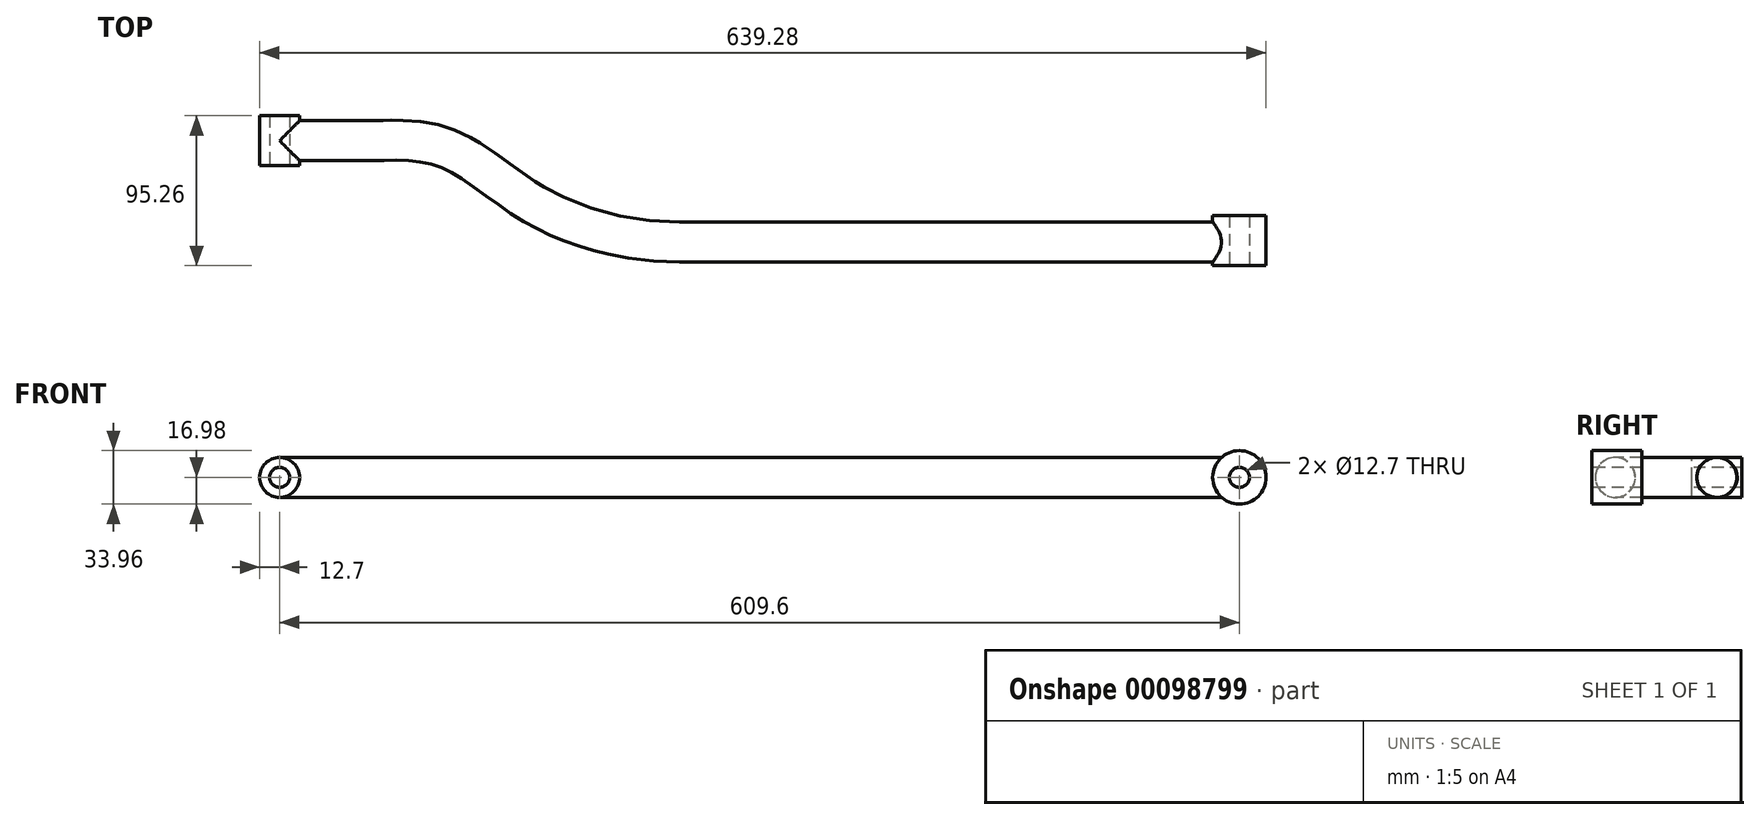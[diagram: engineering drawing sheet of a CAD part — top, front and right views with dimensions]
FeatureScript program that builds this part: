
annotation { "Feature Type Name" : "Feature", "Feature Type Description" : "" }
export const myFeature = defineFeature(function(context is Context, id is Id, definition is map)
    precondition{}
    {
        {
            var Q0;
            Q0=qCreatedBy(makeId("Front.planeOp"),FACE);
            var sketch = newSketch(context, id + "F0", { "sketchPlane" : qUnion([Q0])});
            skCircle(sketch, "E0", {"center": v(0, 0) * mm, "radius": 12.7 * mm});
            skSolve(sketch);
        }
        {
            var Q0;
            Q0=qCreatedBy(makeId("Right.planeOp"),FACE);
            var sketch = newSketch(context, id + "F1", { "sketchPlane" : qUnion([Q0])});
            skCircle(sketch, "E1", {"center": v(0, 0) * mm, "radius": 12.7 * mm});
            skSolve(sketch);
        }
        {
            var Q0;
            Q0=qCreatedBy(makeId("Top.planeOp"),FACE);
            var sketch = newSketch(context, id + "F2", { "sketchPlane" : qUnion([Q0])});
            skLineSegment(sketch, "E2", {"start": v(436.7, -63.5) * mm, "end": v(492.47, -63.5) * mm});
            skSolve(sketch);
        }
        {
            var Q0;
            Q0=sQuery(id+"F2.wireOp",EDGE,"E2");
            cPlane(context, id + "F3", {"entities" : qUnion([Q0]), "cplaneType" : CPlaneType.LINE_ANGLE, "offset" : 152.4 * mm, "angle" : 0 * degree, "width" : 152.4 * mm, "height" : 152.4 * mm});
        }
        {
            var Q0;
            Q0=qCreatedBy(id+"F3.planeOp",FACE);
            var sketch = newSketch(context, id + "F4", { "sketchPlane" : qUnion([Q0])});
            skCircle(sketch, "E3", {"center": v(-609.6, 0) * mm, "radius": 16.98 * mm});
            skSolve(sketch);
        }
        {
            var Q0;
            Q0 = qSketchRegion(id + "F4", true);
            extrude(context, id + "F5", {"entities" : qUnion([Q0]), "depth" : 31.75 * mm, "symmetric" : true});
        }
        {
            var Q0;
            Q0=qCreatedBy(makeId("Top.planeOp"),FACE);
            var sketch = newSketch(context, id + "F6", { "sketchPlane" : qUnion([Q0])});
            skLineSegment(sketch, "E4", {"start": v(0, 0) * mm, "end": v(50.8, 0) * mm});
            skLineSegment(sketch, "E5", {"start": v(609.6, -64.38) * mm, "end": v(254, -64.38) * mm});
            skFitSpline(sketch, "E6", {"points": [v(50.8, 0) * mm, v(105.04, -4.35) * mm, v(163.67, -41.6) * mm, v(254, -64.38) * mm], "startDerivative": vector(192.35, 0) * mm, "endDerivative": vector(257.52, 0) * mm});
            skSolve(sketch);
        }
        {
            var Q0;
            Q0=makeQuery(id+"F1.imprint","IMPRINT",FACE,{"disambiguationData":[TD([[makeQuery(id+"F1.imprint","IMPRINT",EDGE,{"derivedFrom":sQuery(id+"F1.wireOp",EDGE,"E1")}),1.0]])]});
            var Q1;
            Q1=sQuery(id+"F6.wireOp",EDGE,"E4");
            var Q2;
            Q2=sQuery(id+"F6.wireOp",EDGE,"E6");
            var Q3;
            Q3=sQuery(id+"F6.wireOp",EDGE,"E5");
            sweep(context, id + "F7", {"operationType" : NewBodyOperationType.ADD, "profiles" : qUnion([Q0]), "path" : qUnion([Q1, Q2, Q3])});
        }
        {
            var Q0;
            Q0 = qSketchRegion(id + "F0", true);
            extrude(context, id + "F8", {"entities" : qUnion([Q0]), "operationType" : NewBodyOperationType.ADD, "depth" : 31.75 * mm, "symmetric" : true});
        }
        {
            var Q0;
            Q0=makeQuery(id+"F8.opExtrude","CAP_FACE",FACE,{"disambiguationData":[OSD([sQuery(id+"F0.wireOp",EDGE,"E0")])],"isStart":false});
            var sketch = newSketch(context, id + "F9", { "sketchPlane" : qUnion([Q0])});
            skCircle(sketch, "E7", {"center": v(0, 0) * mm, "radius": 6.35 * mm});
            skSolve(sketch);
        }
        {
            var Q0;
            Q0 = qSketchRegion(id + "F9", true);
            extrude(context, id + "F10", {"entities" : qUnion([Q0]), "operationType" : NewBodyOperationType.REMOVE, "oppositeDirection" : true, "depth" : 50.8 * mm});
        }
        {
            var Q0;
            Q0=makeQuery(id+"F5.opExtrude","CAP_FACE",FACE,{"disambiguationData":[OSD([sQuery(id+"F4.wireOp",EDGE,"E3")])],"isStart":true});
            var sketch = newSketch(context, id + "F11", { "sketchPlane" : qUnion([Q0])});
            skCircle(sketch, "E8", {"center": v(609.6, 0) * mm, "radius": 6.35 * mm});
            skSolve(sketch);
        }
        {
            var Q0;
            Q0 = qSketchRegion(id + "F11", true);
            extrude(context, id + "F12", {"entities" : qUnion([Q0]), "operationType" : NewBodyOperationType.REMOVE, "oppositeDirection" : true, "depth" : 50.8 * mm});
        }
    });
